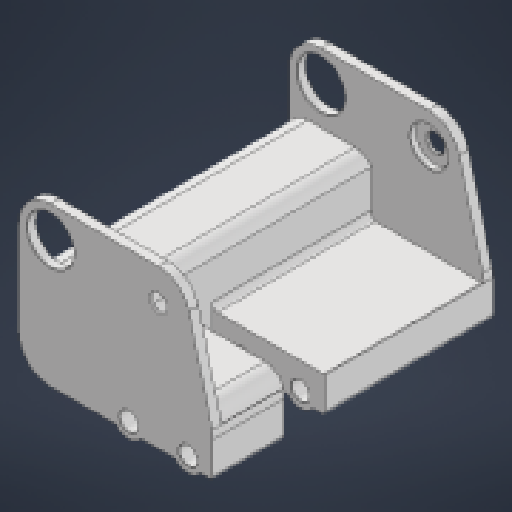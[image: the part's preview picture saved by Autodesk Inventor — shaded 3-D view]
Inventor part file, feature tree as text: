
AUTODESK INVENTOR PART (.ipt)
format: ipt  version: 2024.1 (Build 281209000, 209)  size: 363,520 bytes
history: native  units: in
note: dims shown in document units (in); Inventor stores cm internally (conversion verified against a paired STEP export)
features: extrude x10, sketch x9, reference x8, projected_geometry x5, other x4, chamfer x3, fillet x1
ambient origin geometry x8: Origin, YZ Plane, XZ Plane, XY Plane, X Axis, Y Axis, Z Axis, Center Point
bodies: Solid1 (feature_tree)
feature tree (40):
  extrude  "Extrusion1"  Depth=0.12in
  extrude  "Extrusion2"  Depth=0.42in
  chamfer  "Chamfer1"  Distance=0.0625in
  extrude  "Extrusion3"  Depth=0.0417in TaperAngle=0.0deg
  fillet  "Fillet1"  Radius=0.41in
  extrude  "Extrusion4"  Depth=0.125in
  extrude  "Extrusion5"  Depth=0.276in TaperAngle=0.0deg
  extrude  "Extrusion6"  Depth=0.0625in TaperAngle=0.0deg
  extrude  "Extrusion7"  Depth=0.125in TaperAngle=45.0deg
  chamfer  "Chamfer2"  Distance=0.12in
  sketch  "Sketch8"  dims[d20=1.0545in d21=0.0in d22=0.0625in d23=0.0in]
  extrude  "Extrusion8"  Depth=0.125in
  extrude  "Extrusion9"  Depth=0.125in
  extrude  "Extrusion10"  Depth=0.125in
  chamfer  "Chamfer3"  Distance=0.0417in
  sketch  "Sketch1"  dims[d0=0.005in d1=0.12in]
  reference  "Reference1"
  reference  "Reference2"
  reference  "Reference3"
  sketch  "Sketch2"  dims[d2=0.42in d3=0.42in]
  sketch  "Sketch3"  dims[d4=0.42in d5=0.0625in d6=0.0in]
  projected_geometry  "Projected Loop1"
  reference  "Reference5"
  sketch  "Sketch4"  dims[d7=0.25in d8=0.0417in d9=0.0in]
  reference  "Reference6"
  projected_geometry  "Projected Loop2"
  sketch  "Sketch5"  dims[d10=0.005in d11=0.125in d12=45.0deg d13=0.41in d14=0.0in]
  reference  "Reference7"
  projected_geometry  "Projected Loop3"
  projected_geometry  "Projected Loop4"
  reference  "Reference8"
  sketch  "Sketch6"  dims[d15=0.125in d16=0.25in]
  projected_geometry  "Projected Loop5"
  sketch  "Sketch7"  dims[d17=0.005in d18=0.276in d19=0.0in]
  reference  "Reference9"
  sketch  "Sketch9"  dims[d24=0.0417in d25=0.0in d26=0.005in d27=0.125in d28=45.0deg d29=0.12in d30=0.2in d31=0.12in d32=0.2in d33=0.0417in d34=0.0in d35=1.0in d36=0.0in d37=0.3in d38=0.0in d39=0.005in d40=0.125in d41=45.0deg]
  other  "<userpath>\Documents\School\FallCAD\Bio\Bio.iam"
  other  "Bio.iam"
  other  "Bio12tNew:1"
  other  "Servo HS425BB:1"
